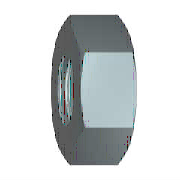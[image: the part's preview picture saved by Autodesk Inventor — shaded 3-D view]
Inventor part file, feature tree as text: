
AUTODESK INVENTOR PART (.ipt)
format: ipt  version: 2022 (Build 260153000, 153)  size: 165,376 bytes
history: native  units: mm (DEFAULTED — no unit token found)
features: sketch x3, extrude x1, chamfer x1, hole x1, other x1, plane x1
ambient origin geometry x7: Origin, YZ Plane, XZ Plane, X Axis, Y Axis, Z Axis, Center Point
bodies: Solid1 (feature_tree)
feature tree (8):
  extrude  "Cuerpo"  Depth=5.2mm
  chamfer  "Chaflán1"  Angle=30.0deg  [1 undecoded]
  hole  "Rosca"  [1 undecoded]
  other  "Work Axis1"
  plane  "Work Plane1"
  sketch  "Boceto1"  dims[d0=11.547005mm d1=5.2mm]
  sketch  "Boceto2"  dims[d2=0.0mm]
  sketch  "Boceto3"  dims[d3=30.0deg d4=30.0deg d5=8.9mm d6=8.9mm d7=90.0deg d25=4.917mm d26=6.0mm d27=4.0mm d28=2.0mm d29=14.3117mm d30=8.0mm d31=20.594885mm d8=0.541266mm d9=30.0deg d10=0.541266mm d11=30.0deg d13=0.0mm d14=0.0mm d39=0.0mm d40=0.541266mm d41=0.541266mm d42=0.0mm]
note: 2 required parameter values undecoded (feature->parameter linkage not recoverable at this tier; creation-order binding heuristic only, values carry confidence <= 0.55)
